# Revit family: Deca_Barra de apoio 70cm_Conforto_2310.070
name_source: partatom
category: Plumbing Fixtures
units: mm (PartAtom-declared; Revit-internal decimal feet)

## family parameters
Cut with Voids When Loaded = No
Host = Face
Part Type = Normal
Room Calculation Point = No
Round Connector Dimension = Use Diameter
Shared = No

## types (2) — shared parameters
Acompanha o Produto = Acompanha Parafusos e Buchas para fixação para alvenaria
Aprovado por = quattroD
Atendimento ao Cliente = 0800-0117073
Categoria = ACESSORIOS
Composição Anel Vedação = -
Composição Assento = -
Composição Componente = -
Consumo = -
Cor Interna = -
Cor Secundária = -
Cores Componente = -
Criado por = quattroD
Código Pai = 2310.070
Default Elevation = 750 mm  [stored 2.46063 ft]
Description = Barra de apoio 70cm
Informações Complementares = -
Itens de Instalação = -
Linha = Conforto
Manufacturer = Deca
Norma = NBR9050
Pressão máx. funcionamento = -
Pressão mín. Aquec. Acúmulo = -
Pressão mín. Aquec. Passagem = -
Pressão mín. funcionamento = -
Saída de Esgoto = -
Segmento = Banheiro Médio
Tipo de dispositivo economizador = -
Tipo de mecanismo utilizado = -
Tipo de rosca de entrada = -
Tipo de rosca de saída = -
URL = www.deca.com.br
Vazão na Pressão máx. (L/min) = -
Vazão na Pressão mín. (L/min) = -
zero-valued in all types: CWFU, WFU

## per-type parameters (varying)
| type | Composição Básica | Cor Principal | Material | Model | Peso Líquido (Kg) |
| 2310.E.070.BR_Branco | Liga de Cobre (bronze e latão),Plásticos de Engenharia,Elastômeros | Branco | Deca_Nylon/PVC | 2310.E.070.BR | 1.83 |
| 2310.I.070.POL_Aço Polido | Aço Inoxidável | Aço Polido | Deca_Aço Polido | 2310.I.070.POL | 1.355 |

note: [stored X ft] marks values corroborated as IEEE doubles in the binary element streams (Revit-internal decimal feet)

## geometry (parser evidence)
native form markers: Sweep x1
no freeform markers — native parametric forms only
